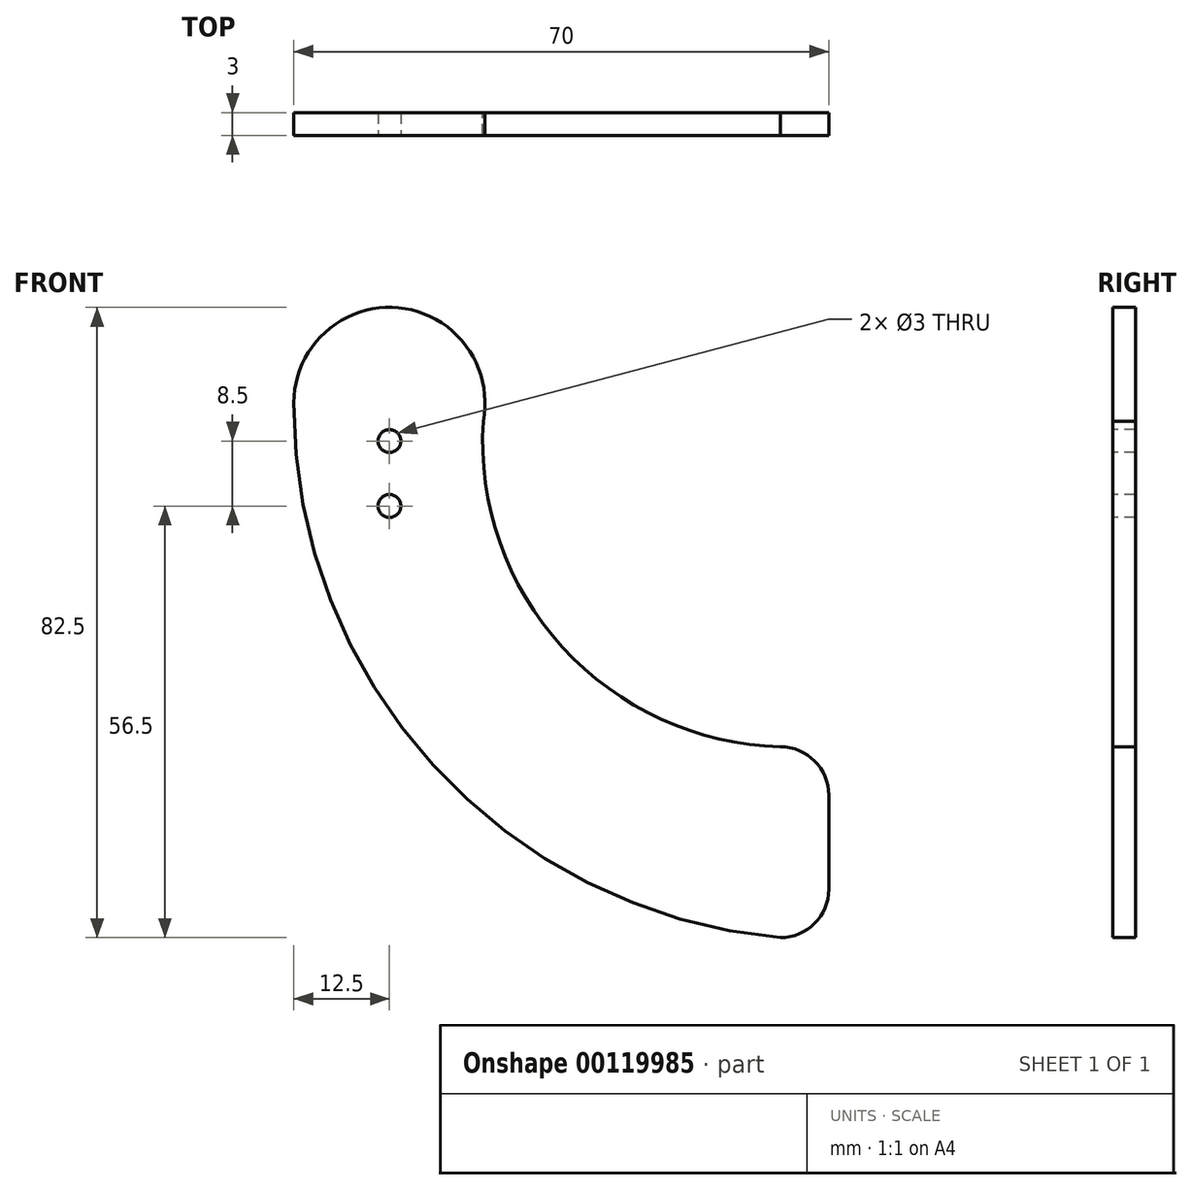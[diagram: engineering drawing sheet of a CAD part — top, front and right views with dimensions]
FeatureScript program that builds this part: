
annotation { "Feature Type Name" : "Feature", "Feature Type Description" : "" }
export const myFeature = defineFeature(function(context is Context, id is Id, definition is map)
    precondition{}
    {
        {
            var Q0;
            Q0=qCreatedBy(makeId("Front.planeOp"),FACE);
            var sketch = newSketch(context, id + "F0", { "sketchPlane" : qUnion([Q0])});
            skCircle(sketch, "E0", {"center": v(0, 0) * mm, "radius": 12.5 * mm});
            skLineSegment(sketch, "E1", {"start": v(-12.5, 0) * mm, "end": v(-12.5, -63.65) * mm});
            skLineSegment(sketch, "E2", {"start": v(-6.15, -70) * mm, "end": v(51.15, -70) * mm});
            skLineSegment(sketch, "E3", {"start": v(57.5, -63.65) * mm, "end": v(57.5, -51.35) * mm});
            skLineSegment(sketch, "E4", {"start": v(12.46, 1) * mm, "end": v(12.46, -1) * mm});
            skLineSegment(sketch, "E5.1.2", {"start": v(-12.46, -1) * mm, "end": v(-12.46, 1) * mm});
            skLineSegment(sketch, "E5.anchor1", {"start": v(0, 0) * mm, "end": v(12.46, -1) * mm, "construction": true});
            skLineSegment(sketch, "E5.anchor2", {"start": v(0, 0) * mm, "end": v(-12.46, 1) * mm, "construction": true});
            skPoint(sketch, "E6.visualSharp", {"position": v(12.5, -45) * mm});
            skPoint(sketch, "E7.visualSharp", {"position": v(-12.5, -70) * mm});
            skArc(sketch, "E7.filletArc", {"start": v(-12.5, -63.65) * mm, "mid": v(-10.64, -68.14) * mm, "end": v(-6.15, -70) * mm});
            skPoint(sketch, "E8.visualSharp", {"position": v(57.5, -70) * mm});
            skArc(sketch, "E8.filletArc", {"start": v(51.15, -70) * mm, "mid": v(55.64, -68.14) * mm, "end": v(57.5, -63.65) * mm});
            skPoint(sketch, "E9.visualSharp", {"position": v(57.5, -45) * mm});
            skArc(sketch, "E9.filletArc", {"start": v(57.5, -51.35) * mm, "mid": v(55.64, -46.86) * mm, "end": v(51.15, -45) * mm});
            skCircle(sketch, "E10", {"center": v(0, 0) * mm, "radius": 1.5 * mm});
            skArc(sketch, "E11", {"start": v(12.5, 0) * mm, "mid": v(21.84, -31.08) * mm, "end": v(51.15, -45) * mm});
            skArc(sketch, "E12", {"start": v(-12.5, 0) * mm, "mid": v(5.7, -47.38) * mm, "end": v(51.15, -70) * mm});
            skSolve(sketch);
        }
        {
            var Q0;
            {var subQ0=sQuery(id+"F0.wireOp",EDGE,"E12");var subQ1=sQuery(id+"F0.wireOp",EDGE,"E1");var subQ3=makeQuery(id+"F0.imprint","INTERSECT",VERTEX,{"derivedFrom":[subQ1,subQ0]});Q0=makeQuery(id+"F0.imprint","IMPRINT",FACE,{"disambiguationData":[TD([[makeQuery(id+"F0.imprint","IMPRINT",EDGE,{"disambiguationData":[TD([[subQ3,1.0]])],"derivedFrom":subQ1}),-1.0]])]});}
            var Q1;
            {var subQ0=sQuery(id+"F0.wireOp",EDGE,"E12");var subQ1=sQuery(id+"F0.wireOp",EDGE,"E2");var subQ3=makeQuery(id+"F0.imprint","INTERSECT",VERTEX,{"derivedFrom":[subQ1,subQ0]});Q1=makeQuery(id+"F0.imprint","IMPRINT",FACE,{"disambiguationData":[TD([[makeQuery(id+"F0.imprint","IMPRINT",EDGE,{"disambiguationData":[TD([[subQ3,-1.0]])],"derivedFrom":subQ1}),-1.0]])]});}
            var Q2;
            {var subQ0=sQuery(id+"F0.wireOp",EDGE,"E4");var subQ1=sQuery(id+"F0.wireOp",EDGE,"E0");var subQ2=makeQuery(id+"F0.imprint","INTERSECT",VERTEX,{"disambiguationData":[OD(0.0)],"derivedFrom":[subQ1,subQ0]});Q2=makeQuery(id+"F0.imprint","IMPRINT",FACE,{"disambiguationData":[TD([[makeQuery(id+"F0.imprint","IMPRINT",EDGE,{"disambiguationData":[TD([[subQ2,1.0]])],"derivedFrom":subQ1}),1.0]])]});}
            var Q3;
            {var subQ2=sQuery(id+"F0.wireOp",EDGE,"E5.1.2");Q3=makeQuery(id+"F0.imprint","IMPRINT",FACE,{"disambiguationData":[TD([[makeQuery(id+"F0.imprint","IMPRINT",EDGE,{"derivedFrom":subQ2}),1.0]])]});}
            var Q4;
            {var subQ0=sQuery(id+"F0.wireOp",EDGE,"E4");var subQ1=sQuery(id+"F0.wireOp",EDGE,"E0");var subQ2=makeQuery(id+"F0.imprint","INTERSECT",VERTEX,{"disambiguationData":[OD(1.0)],"derivedFrom":[subQ1,subQ0]});Q4=makeQuery(id+"F0.imprint","IMPRINT",FACE,{"disambiguationData":[TD([[makeQuery(id+"F0.imprint","IMPRINT",EDGE,{"disambiguationData":[TD([[subQ2,1.0]])],"derivedFrom":subQ1}),1.0]])]});}
            var Q5;
            {var subQ0=sQuery(id+"F0.wireOp",EDGE,"E4");var subQ1=sQuery(id+"F0.wireOp",EDGE,"E0");var subQ2=makeQuery(id+"F0.imprint","INTERSECT",VERTEX,{"disambiguationData":[OD(1.0)],"derivedFrom":[subQ1,subQ0]});Q5=makeQuery(id+"F0.imprint","IMPRINT",FACE,{"disambiguationData":[TD([[makeQuery(id+"F0.imprint","IMPRINT",EDGE,{"disambiguationData":[TD([[subQ2,-1.0]])],"derivedFrom":subQ1}),1.0]])]});}
            var Q6;
            {var subQ0=sQuery(id+"F0.wireOp",EDGE,"E5.1.2");Q6=makeQuery(id+"F0.imprint","IMPRINT",FACE,{"disambiguationData":[TD([[makeQuery(id+"F0.imprint","IMPRINT",EDGE,{"derivedFrom":subQ0}),-1.0]])]});}
            var Q7;
            Q7=makeQuery(id+"F0.imprint","IMPRINT",FACE,{"disambiguationData":[TD([[makeQuery(id+"F0.imprint","IMPRINT",EDGE,{"derivedFrom":sQuery(id+"F0.wireOp",EDGE,"E3")}),1.0]])]});
            var Q8;
            Q8=makeQuery(id+"F0.imprint","IMPRINT",FACE,{"disambiguationData":[TD([[makeQuery(id+"F0.imprint","IMPRINT",EDGE,{"derivedFrom":sQuery(id+"F0.wireOp",EDGE,"E10")}),1.0]])]});
            extrude(context, id + "F1", {"entities" : qUnion([Q0, Q1, Q2, Q3, Q4, Q5, Q6, Q7, Q8]), "depth" : 3 * mm});
        }
        {
            var Q0;
            Q0=makeQuery(id+"F1.opExtrude","CAP_FACE",FACE,{"disambiguationData":[OSD([sQuery(id+"F0.wireOp",EDGE,"E0"),sQuery(id+"F0.wireOp",EDGE,"E1"),sQuery(id+"F0.wireOp",EDGE,"E2"),sQuery(id+"F0.wireOp",EDGE,"E3"),sQuery(id+"F0.wireOp",EDGE,"Qa6hpvG3-VeAc-d2hB-WOSB-8mIrRalq00KK"),sQuery(id+"F0.wireOp",EDGE,"1B4x0ZdV-p1ow-g5zO-RRGP-5L7Yw6DpvPT2"),sQuery(id+"F0.wireOp",EDGE,"P5pQIiWr-d6a9-dL8I-5OkA-PKon0IUBUqMW"),sQuery(id+"F0.wireOp",EDGE,"O7sfM2wC-z6aj-ywW9-o4Z8-QTpTmjdLFcAP"),sQuery(id+"F0.wireOp",EDGE,"E5.1.0"),sQuery(id+"F0.wireOp",EDGE,"E5.1.1"),sQuery(id+"F0.wireOp",EDGE,"E5.2.0"),sQuery(id+"F0.wireOp",EDGE,"E5.2.1"),sQuery(id+"F0.wireOp",EDGE,"E5.3.0"),sQuery(id+"F0.wireOp",EDGE,"E5.3.1"),sQuery(id+"F0.wireOp",EDGE,"E5.4.0"),sQuery(id+"F0.wireOp",EDGE,"E5.4.1"),sQuery(id+"F0.wireOp",EDGE,"E5.5.0"),sQuery(id+"F0.wireOp",EDGE,"E5.5.1"),sQuery(id+"F0.wireOp",EDGE,"E5.6.0"),sQuery(id+"F0.wireOp",EDGE,"E5.6.1"),sQuery(id+"F0.wireOp",EDGE,"E5.7.0"),sQuery(id+"F0.wireOp",EDGE,"E5.7.1"),sQuery(id+"F0.wireOp",EDGE,"E5.8.0"),sQuery(id+"F0.wireOp",EDGE,"E5.8.1"),sQuery(id+"F0.wireOp",EDGE,"E5.9.0"),sQuery(id+"F0.wireOp",EDGE,"E5.9.1"),sQuery(id+"F0.wireOp",EDGE,"E5.10.0"),sQuery(id+"F0.wireOp",EDGE,"E5.10.1"),sQuery(id+"F0.wireOp",EDGE,"E5.11.0"),sQuery(id+"F0.wireOp",EDGE,"E5.11.1"),sQuery(id+"F0.wireOp",EDGE,"E5.12.0"),sQuery(id+"F0.wireOp",EDGE,"E5.12.1"),sQuery(id+"F0.wireOp",EDGE,"E5.13.0"),sQuery(id+"F0.wireOp",EDGE,"E5.13.1"),sQuery(id+"F0.wireOp",EDGE,"E5.14.0"),sQuery(id+"F0.wireOp",EDGE,"E5.14.1"),sQuery(id+"F0.wireOp",EDGE,"E5.15.0"),sQuery(id+"F0.wireOp",EDGE,"E5.15.1"),sQuery(id+"F0.wireOp",EDGE,"E5.16.0"),sQuery(id+"F0.wireOp",EDGE,"E5.16.1"),sQuery(id+"F0.wireOp",EDGE,"E5.17.0"),sQuery(id+"F0.wireOp",EDGE,"E5.17.1"),sQuery(id+"F0.wireOp",EDGE,"E5.18.0"),sQuery(id+"F0.wireOp",EDGE,"E5.18.1"),sQuery(id+"F0.wireOp",EDGE,"E5.19.0"),sQuery(id+"F0.wireOp",EDGE,"E5.19.1"),sQuery(id+"F0.wireOp",EDGE,"E6.filletArc"),sQuery(id+"F0.wireOp",EDGE,"E7.filletArc"),sQuery(id+"F0.wireOp",EDGE,"E8.filletArc"),sQuery(id+"F0.wireOp",EDGE,"E9.filletArc")])],"isStart":false});
            var sketch = newSketch(context, id + "F2", { "sketchPlane" : qUnion([Q0])});
            skLineSegment(sketch, "E13", {"start": v(0, 0) * mm, "end": v(0, -5) * mm});
            skLineSegment(sketch, "E14", {"start": v(0, -5) * mm, "end": v(0, -13.5) * mm});
            skCircle(sketch, "E15", {"center": v(0, -13.5) * mm, "radius": 1.5 * mm});
            skCircle(sketch, "E16", {"center": v(0, -5) * mm, "radius": 1.5 * mm});
            skSolve(sketch);
        }
        {
            var Q0;
            Q0 = qSketchRegion(id + "F2", true);
            extrude(context, id + "F3", {"entities" : qUnion([Q0]), "operationType" : NewBodyOperationType.REMOVE, "oppositeDirection" : true, "depth" : 762 * mm, "symmetric" : true});
        }
    });
